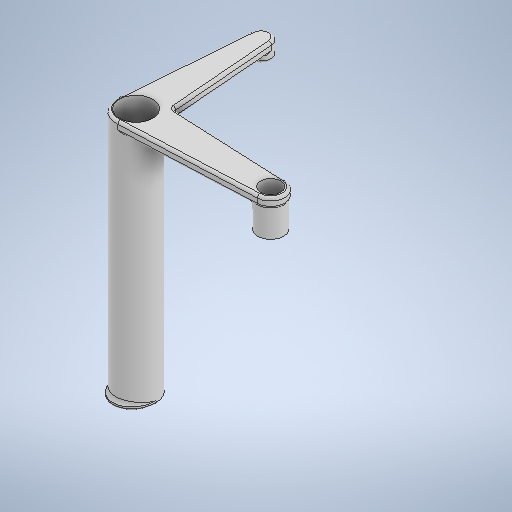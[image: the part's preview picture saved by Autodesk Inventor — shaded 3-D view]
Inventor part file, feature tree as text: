
AUTODESK INVENTOR PART (.ipt)
format: ipt  version: 2025 (Build 290162000, 162)  size: 757,760 bytes
history: native  units: mm
features: extrude x6, other x4, fillet x3, sketch x3
ambient origin geometry x8: Origin, YZ Plane, XZ Plane, XY Plane, X Axis, Y Axis, Z Axis, Center Point
bodies: Body1 (feature_tree)
feature tree (16):
  other  "ソリッド1"
  extrude  "軸"  Depth=12.0mm
  extrude  "アーム"  Depth=10.0mm
  extrude  "接合部"  Depth=73.0mm TaperAngle=0.0deg
  extrude  "ねじ頭"  Depth=45.5mm
  extrude  "押し出し5"  Depth=12.0mm
  fillet  "フィレット1"  Radius=3.0mm
  fillet  "フィレット3"  Radius=7.8mm
  extrude  "押し出し6"  Depth=40.5mm
  fillet  "フィレット4"  Radius=8.0mm
  other  "軸スケッチ"
  other  "アームスケッチ"
  other  "接合部スケッチ"
  sketch  "スケッチ4"
  sketch  "スケッチ5"
  sketch  "スケッチ6"
